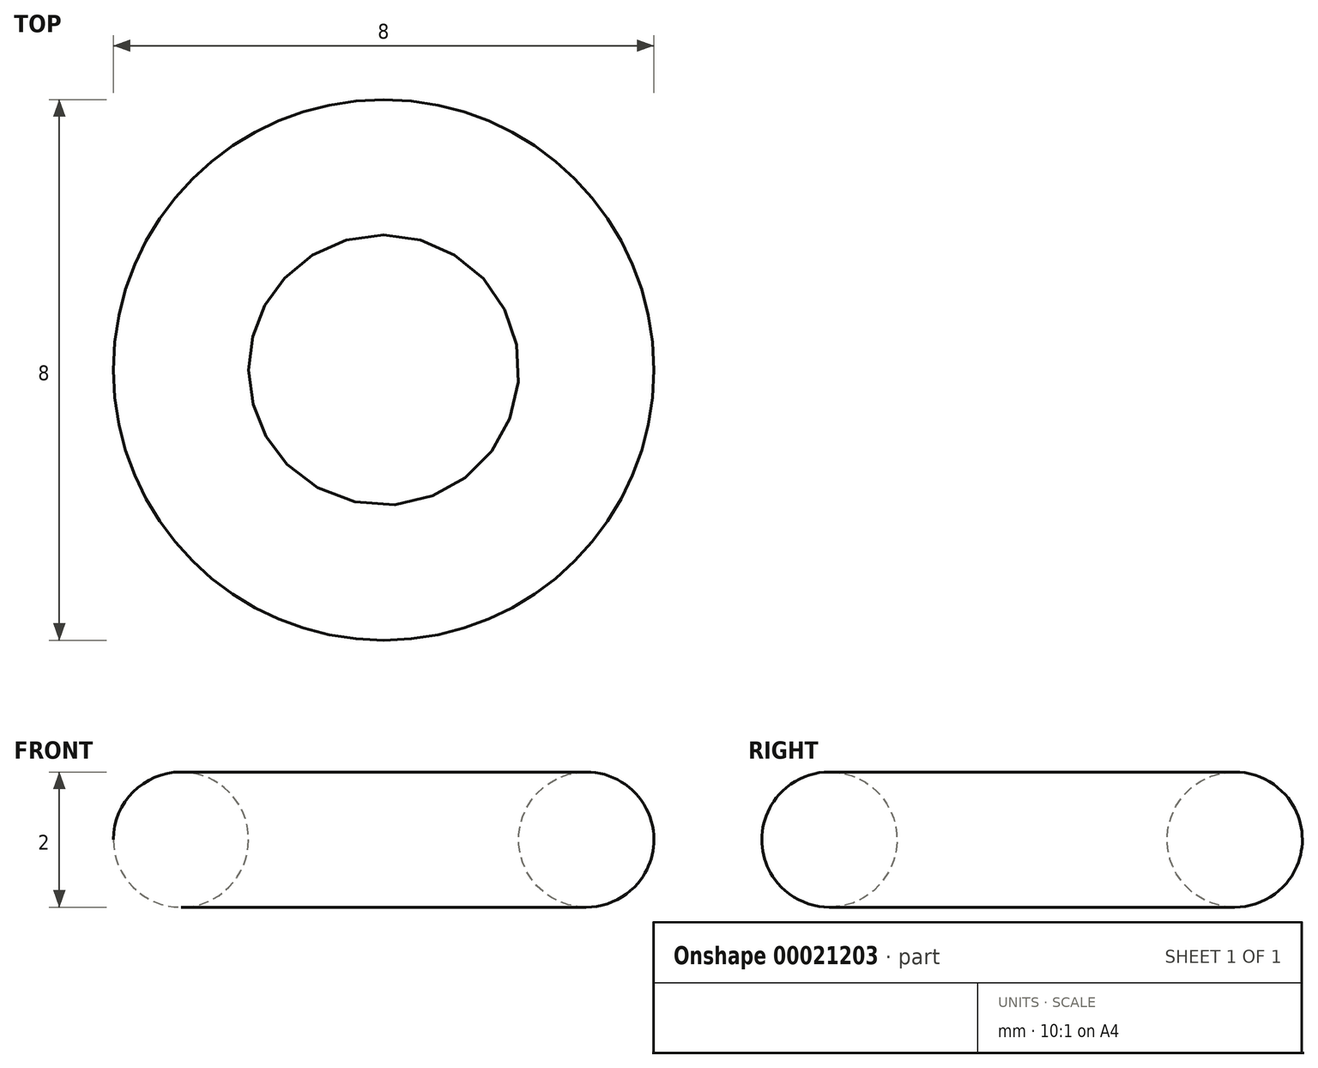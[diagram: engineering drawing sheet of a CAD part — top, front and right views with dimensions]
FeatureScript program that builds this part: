
annotation { "Feature Type Name" : "Feature", "Feature Type Description" : "" }
export const myFeature = defineFeature(function(context is Context, id is Id, definition is map)
    precondition{}
    {
        {
            var Q0;
            Q0=qCreatedBy(makeId("Front.planeOp"),FACE);
            var sketch = newSketch(context, id + "F0", { "sketchPlane" : qUnion([Q0])});
            skLineSegment(sketch, "E0", {"start": v(0, 0) * mm, "end": v(0, 2.51) * mm, "construction": true});
            skCircle(sketch, "E1", {"center": v(3, 0) * mm, "radius": 1 * mm});
            skSolve(sketch);
        }
        {
            var Q0;
            Q0=qSketchRegion(id+"F0",true);
            var Q1;
            Q1=sQuery(id+"F0.wireOp",EDGE,"E0");
            revolve(context, id + "F1", {"entities" : qUnion([Q0]), "axis" : qUnion([Q1]), "revolveType" : RevolveType.FULL});
        }
    });
